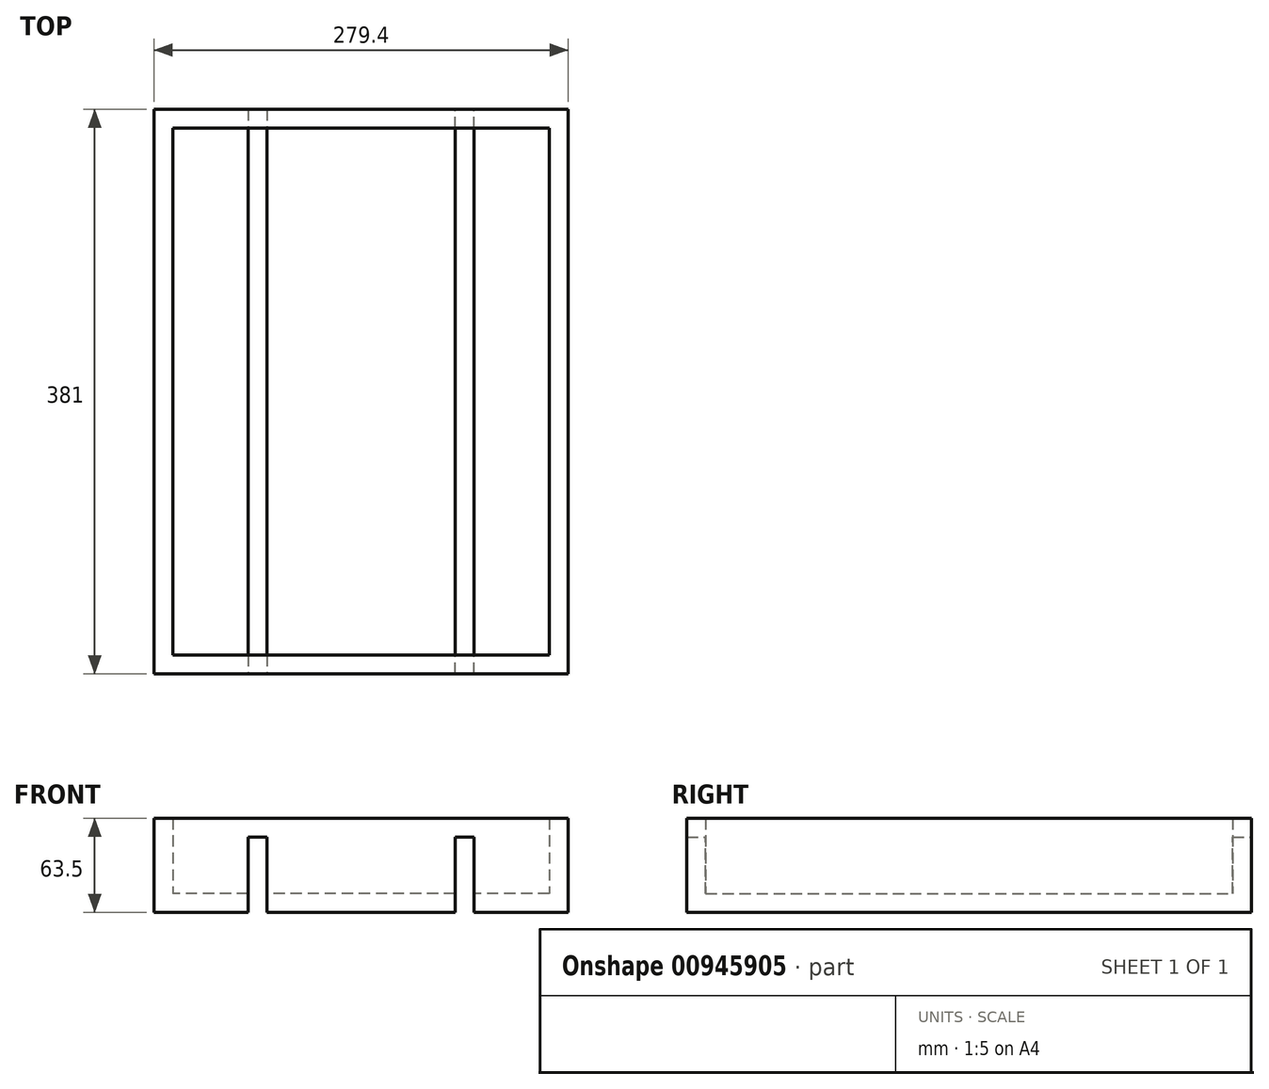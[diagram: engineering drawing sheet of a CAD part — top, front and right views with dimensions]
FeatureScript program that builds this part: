
annotation { "Feature Type Name" : "Feature", "Feature Type Description" : "" }
export const myFeature = defineFeature(function(context is Context, id is Id, definition is map)
    precondition{}
    {
        {
            var Q0;
            Q0=qCreatedBy(makeId("Top.planeOp"),FACE);
            var sketch = newSketch(context, id + "F0", { "sketchPlane" : qUnion([Q0])});
            skLineSegment(sketch, "E0.bottom", {"start": v(139.7, 190.5) * mm, "end": v(-139.7, 190.5) * mm});
            skLineSegment(sketch, "E0.top", {"start": v(139.7, -190.5) * mm, "end": v(-139.7, -190.5) * mm});
            skLineSegment(sketch, "E0.left", {"start": v(139.7, 190.5) * mm, "end": v(139.7, -190.5) * mm});
            skLineSegment(sketch, "E0.right", {"start": v(-139.7, 190.5) * mm, "end": v(-139.7, -190.5) * mm});
            skPoint(sketch, "E0.middle", {"position": v(0, 0) * mm});
            skLineSegment(sketch, "E1.bottom", {"start": v(127, 177.8) * mm, "end": v(-127, 177.8) * mm});
            skLineSegment(sketch, "E1.top", {"start": v(127, -177.8) * mm, "end": v(-127, -177.8) * mm});
            skLineSegment(sketch, "E1.left", {"start": v(127, 177.8) * mm, "end": v(127, -177.8) * mm});
            skLineSegment(sketch, "E1.right", {"start": v(-127, 177.8) * mm, "end": v(-127, -177.8) * mm});
            skSolve(sketch);
        }
        {
            var Q0;
            Q0=makeQuery(id+"F0.imprint","IMPRINT",FACE,{"disambiguationData":[TD([[makeQuery(id+"F0.imprint","IMPRINT",EDGE,{"derivedFrom":sQuery(id+"F0.wireOp",EDGE,"E0.bottom")}),1.0]])]});
            extrude(context, id + "F1", {"entities" : qUnion([Q0]), "depth" : 50.8 * mm, "offsetDistance" : 25.4 * mm});
        }
        {
            var Q0;
            Q0=makeQuery(id+"F0.imprint","IMPRINT",FACE,{"disambiguationData":[TD([[makeQuery(id+"F0.imprint","IMPRINT",EDGE,{"derivedFrom":sQuery(id+"F0.wireOp",EDGE,"E0.bottom")}),1.0]])]});
            var Q1;
            Q1=makeQuery(id+"F0.imprint","IMPRINT",FACE,{"disambiguationData":[TD([[makeQuery(id+"F0.imprint","IMPRINT",EDGE,{"derivedFrom":sQuery(id+"F0.wireOp",EDGE,"E1.bottom")}),1.0]])]});
            extrude(context, id + "F2", {"entities" : qUnion([Q0, Q1]), "operationType" : NewBodyOperationType.ADD, "oppositeDirection" : true, "depth" : 12.7 * mm, "offsetDistance" : 25.4 * mm});
        }
        {
            var Q0;
            Q0=makeQuery(id+"F2.opExtrude","CAP_FACE",FACE,{"disambiguationData":[OSD([sQuery(id+"F0.wireOp",EDGE,"E0.bottom"),sQuery(id+"F0.wireOp",EDGE,"E0.top"),sQuery(id+"F0.wireOp",EDGE,"E0.left"),sQuery(id+"F0.wireOp",EDGE,"E0.right")])],"isStart":false});
            var sketch = newSketch(context, id + "F3", { "sketchPlane" : qUnion([Q0])});
            skLineSegment(sketch, "E2.bottom", {"start": v(-76.2, -190.5) * mm, "end": v(-63.5, -190.5) * mm});
            skLineSegment(sketch, "E2.top", {"start": v(-76.2, 190.5) * mm, "end": v(-63.5, 190.5) * mm});
            skLineSegment(sketch, "E2.left", {"start": v(-76.2, -190.5) * mm, "end": v(-76.2, 190.5) * mm});
            skLineSegment(sketch, "E2.right", {"start": v(-63.5, -190.5) * mm, "end": v(-63.5, 190.5) * mm});
            skLineSegment(sketch, "E3.bottom", {"start": v(63.5, 190.5) * mm, "end": v(76.2, 190.5) * mm});
            skLineSegment(sketch, "E3.top", {"start": v(63.5, -190.5) * mm, "end": v(76.2, -190.5) * mm});
            skLineSegment(sketch, "E3.left", {"start": v(63.5, 190.5) * mm, "end": v(63.5, -190.5) * mm});
            skLineSegment(sketch, "E3.right", {"start": v(76.2, 190.5) * mm, "end": v(76.2, -190.5) * mm});
            skSolve(sketch);
        }
        {
            var Q0;
            Q0=makeQuery(id+"F3.imprint","IMPRINT",FACE,{"disambiguationData":[TD([[makeQuery(id+"F3.imprint","IMPRINT",EDGE,{"derivedFrom":sQuery(id+"F3.wireOp",EDGE,"E2.bottom")}),-1.0]])]});
            var Q1;
            Q1=makeQuery(id+"F3.imprint","IMPRINT",FACE,{"disambiguationData":[TD([[makeQuery(id+"F3.imprint","IMPRINT",EDGE,{"derivedFrom":sQuery(id+"F3.wireOp",EDGE,"E3.bottom")}),1.0]])]});
            extrude(context, id + "F4", {"entities" : qUnion([Q0, Q1]), "operationType" : NewBodyOperationType.REMOVE, "oppositeDirection" : true, "depth" : 50.8 * mm, "offsetDistance" : 25.4 * mm});
        }
    });
